# Revit family: Walk_in_Door-ELT_Custom_Coolers-French_Style
name_source: partatom
category: Doors
units: mm (PartAtom-declared; Revit-internal decimal feet)

## family parameters
Always vertical = Yes
Classification Number = 23.30.10.00
Cut with Voids When Loaded = No
Host = Wall
Room Calculation Point = No
Shared = No

## types (8) — shared parameters
Analytic Construction = <None>
Define Thermal Properties by = Schematic Type
Frame Material = ELT_White Stucco Embossed
Frame Width = 5 1/2"
Function = Interior
Manufacturer = ELT Custom Coolers
Panel Material = ELT_White Stucco Embossed
Product Page URL = https://eltcoolerdoors.com
Thickness = 4"
URL = https://eltcoolerdoors.com
Wall Closure = By host

## per-type parameters (varying)
| type | Description | Frame Thickness | Height | Jamb Frame | Model | Panel Width | Plug Frame | Rough Height | Rough Width | Width |
| 72" x 84" Cooler, Jamb Frame | Walk in Cooler French Style Door 72"x 84" Prehung with a Retrofit Heated & Jamb Frame for New Construction. | 1 1/2" | 84" | Yes | ELT 72" x 84" | 36" | No | 85" | 71" | 72" |
| 72" x 84" Cooler, Plug Frame | Walk in Cooler French Style Door 72"x 84" Prehung with a Retrofit Heated & Plug Frame for Replacement applications. | 2" | 84" | No | ELT 72" x 84" | 36" | Yes | 84" | 69" | 72" |
| 60" x 78" Cooler, Jamb Frame | Walk in Cooler French Style Door 60"x 78" Prehung with a Retrofit Heated & Jamb Frame for New Construction. | 1 1/2" | 78" | Yes | ELT 60" x 78" | 30" | No | 79" | 59" | 60" |
| 60" x 78" Cooler, Plug Frame | Walk in Cooler French Style Door 60"x 78" Prehung with a Retrofit Heated & Plug Frame for Replacement applications. | 2" | 78" | No | ELT 60" x 78" | 30" | Yes | 78" | 57" | 60" |
| 36" x 78" Cooler, Jamb Frame | Walk in Cooler French Style Door 36"x 78" Prehung with a Retrofit Heated & Jamb Frame for New Construction. | 1 1/2" | 78" | Yes | ELT 36" x 78" | 18" | No | 79" | 35" | 36" |
| 36" x 78" Cooler, Plug Frame | Walk in Cooler French Style Door 36"x 78" Prehung with a Retrofit Heated & Plug Frame for Replacement applications. | 2" | 78" | No | ELT 36" x 78" | 18" | Yes | 78" | 33" | 36" |
| 36" x 78" Freezer, Jamb Frame | Walk in Freezer French Style Door 36"x 78" Prehung with a Retrofit Heated & Jamb Frame for New Construction. | 1 1/2" | 78" | Yes | ELT 36" x 78" | 18" | No | 79" | 35" | 36" |
| 36" x 78" Freezer, Plug Frame | Walk in Freezer French Style Door 36"x 78" Prehung with a Retrofit Heated & Plug Frame for Replacement applications. | 2" | 78" | No | ELT 36" x 78" | 18" | Yes | 78" | 33" | 36" |

## geometry (parser evidence)
native form markers: Sweep x11
no freeform markers — native parametric forms only
